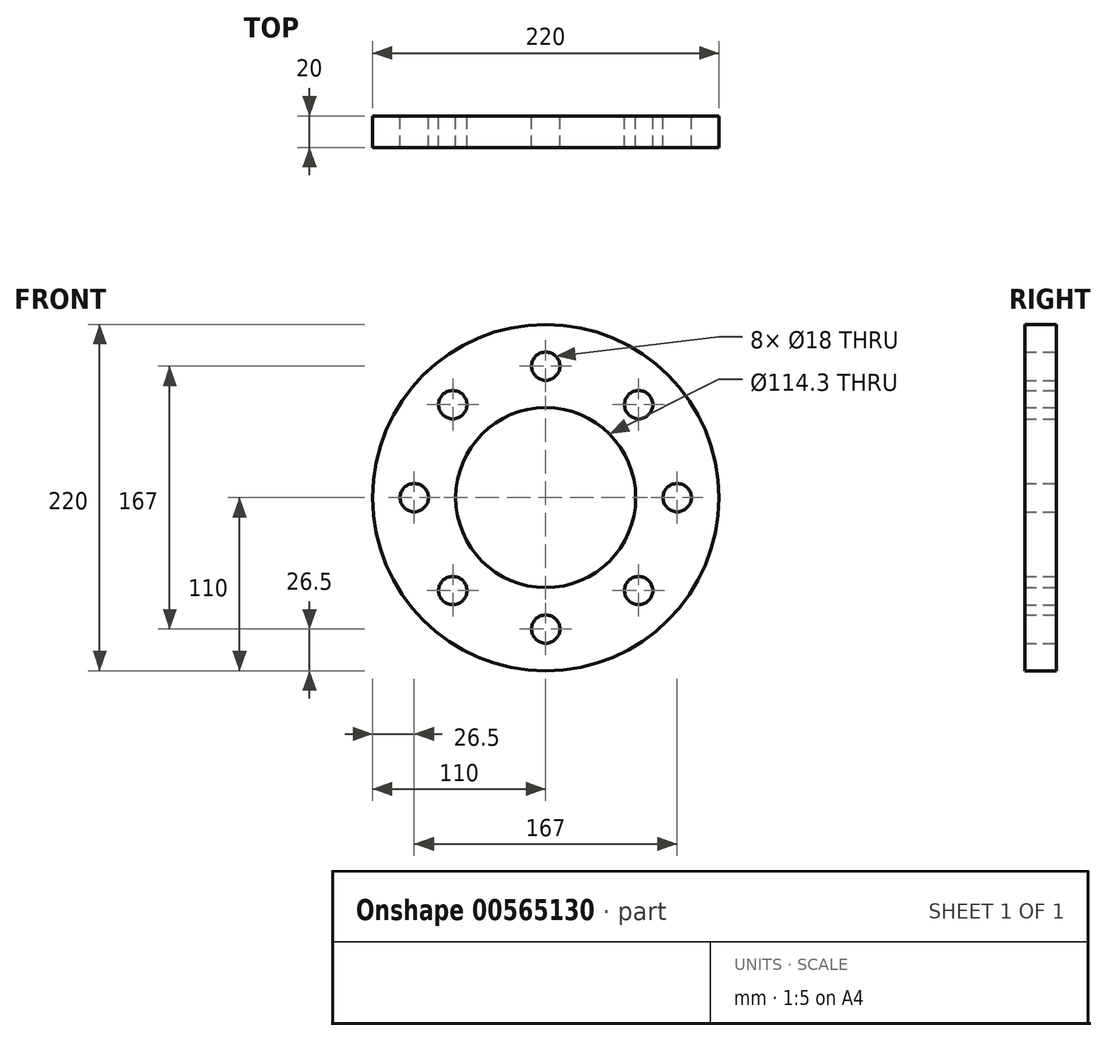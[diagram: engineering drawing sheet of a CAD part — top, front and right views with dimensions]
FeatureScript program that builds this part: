
annotation { "Feature Type Name" : "Feature", "Feature Type Description" : "" }
export const myFeature = defineFeature(function(context is Context, id is Id, definition is map)
    precondition{}
    {
        {
            var Q0;
            Q0=qCreatedBy(makeId("Front.planeOp"),FACE);
            var sketch = newSketch(context, id + "F0", { "sketchPlane" : qUnion([Q0])});
            skCircle(sketch, "E0", {"center": v(0, 0) * mm, "radius": 110 * mm});
            skCircle(sketch, "E1", {"center": v(0, 0) * mm, "radius": 57.15 * mm});
            skCircle(sketch, "E2", {"center": v(0, 0) * mm, "radius": 83.5 * mm, "construction": true});
            skCircle(sketch, "E3", {"center": v(-83.5, 0) * mm, "radius": 9 * mm});
            skCircle(sketch, "E4", {"center": v(0, 83.5) * mm, "radius": 9 * mm});
            skCircle(sketch, "E5", {"center": v(83.5, 0) * mm, "radius": 9 * mm});
            skCircle(sketch, "E6", {"center": v(0, -83.5) * mm, "radius": 9 * mm});
            skLineSegment(sketch, "E7", {"start": v(0, 0) * mm, "end": v(77.78, 77.78) * mm, "construction": true});
            skLineSegment(sketch, "E8", {"start": v(0, 0) * mm, "end": v(-77.78, 77.78) * mm, "construction": true});
            skLineSegment(sketch, "E9", {"start": v(0, 0) * mm, "end": v(77.78, -77.78) * mm, "construction": true});
            skLineSegment(sketch, "E10", {"start": v(0, 0) * mm, "end": v(-77.78, -77.78) * mm, "construction": true});
            skCircle(sketch, "E11", {"center": v(-59.04, 59.04) * mm, "radius": 9 * mm});
            skCircle(sketch, "E12", {"center": v(59.04, 59.04) * mm, "radius": 9 * mm});
            skCircle(sketch, "E13", {"center": v(59.04, -59.04) * mm, "radius": 9 * mm});
            skCircle(sketch, "E14", {"center": v(-59.04, -59.04) * mm, "radius": 9 * mm});
            skSolve(sketch);
        }
        {
            var Q0;
            Q0=makeQuery(id+"F0.imprint","IMPRINT",FACE,{"disambiguationData":[TD([[makeQuery(id+"F0.imprint","IMPRINT",EDGE,{"derivedFrom":sQuery(id+"F0.wireOp",EDGE,"E0")}),1.0]])]});
            extrude(context, id + "F1", {"entities" : qUnion([Q0]), "depth" : 20 * mm, "offsetDistance" : 25 * mm});
        }
    });
